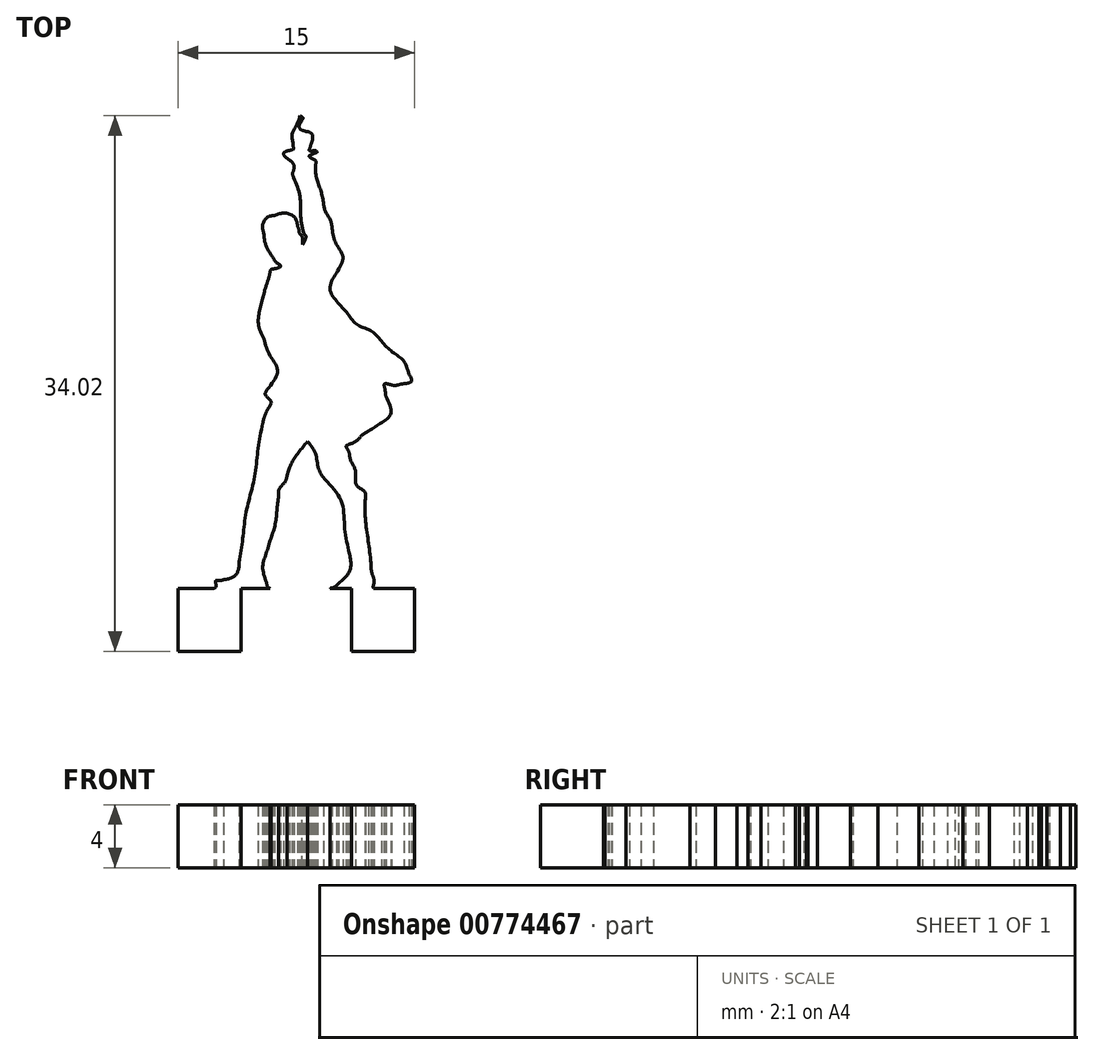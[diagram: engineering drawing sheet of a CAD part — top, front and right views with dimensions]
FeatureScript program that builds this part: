
annotation { "Feature Type Name" : "Feature", "Feature Type Description" : "" }
export const myFeature = defineFeature(function(context is Context, id is Id, definition is map)
    precondition{}
    {
        {
            var Q0;
            Q0=qCreatedBy(makeId("Top.planeOp"),FACE);
            var sketch = newSketch(context, id + "F0", { "sketchPlane" : qUnion([Q0])});
            skFitSpline(sketch, "E0", {"points": [v(-2.9, -14.64) * mm, v(-3.14, -13.66) * mm, v(-2.91, -12.76) * mm, v(-2.63, -11.83) * mm]});
            skFitSpline(sketch, "E1", {"points": [v(-2.63, -11.83) * mm, v(-2.36, -10.96) * mm, v(-2.24, -10.04) * mm, v(-2.13, -9.13) * mm]});
            skFitSpline(sketch, "E2", {"points": [v(-2.13, -9.13) * mm, v(-2.07, -8.64) * mm, v(-1.75, -8.28) * mm, v(-1.6, -7.84) * mm]});
            skFitSpline(sketch, "E3", {"points": [v(-1.6, -7.84) * mm, v(-1.32, -7.06) * mm, v(-0.86, -6.36) * mm, v(-0.3, -5.68) * mm]});
            skFitSpline(sketch, "E4", {"points": [v(-0.3, -5.68) * mm, v(0.23, -6.51) * mm, v(0.42, -7.46) * mm, v(0.97, -8.26) * mm]});
            skFitSpline(sketch, "E5", {"points": [v(0.97, -8.26) * mm, v(1.88, -9.56) * mm, v(2.06, -11.1) * mm, v(2.32, -12.62) * mm]});
            skFitSpline(sketch, "E6", {"points": [v(2.32, -12.62) * mm, v(2.46, -13.46) * mm, v(2.3, -14.07) * mm, v(1.67, -14.7) * mm]});
            skFitSpline(sketch, "E7", {"points": [v(1.67, -14.7) * mm, v(1.47, -14.9) * mm, v(1.3, -14.97) * mm, v(1.12, -15) * mm]});
            skFitSpline(sketch, "E8", {"points": [v(3.9, -15) * mm, v(3.88, -14.98) * mm, v(3.87, -14.94) * mm, v(3.88, -14.89) * mm]});
            skFitSpline(sketch, "E9", {"points": [v(3.88, -14.89) * mm, v(3.92, -14.44) * mm, v(3.79, -14.02) * mm, v(3.74, -13.58) * mm]});
            skFitSpline(sketch, "E10", {"points": [v(3.74, -13.58) * mm, v(3.6, -12.23) * mm, v(3.4, -10.87) * mm, v(3.35, -9.51) * mm]});
            skFitSpline(sketch, "E11", {"points": [v(3.35, -9.51) * mm, v(3.32, -8.87) * mm, v(2.83, -8.49) * mm, v(2.76, -7.9) * mm]});
            skFitSpline(sketch, "E12", {"points": [v(2.76, -7.9) * mm, v(2.71, -7.42) * mm, v(2.48, -6.98) * mm, v(2.36, -6.5) * mm]});
            skFitSpline(sketch, "E13", {"points": [v(2.36, -6.5) * mm, v(2.3, -6.28) * mm, v(2.16, -5.99) * mm, v(2.47, -5.82) * mm]});
            skFitSpline(sketch, "E14", {"points": [v(2.47, -5.82) * mm, v(2.88, -5.6) * mm, v(3.19, -5.26) * mm, v(3.58, -5.01) * mm]});
            skFitSpline(sketch, "E15", {"points": [v(3.58, -5.01) * mm, v(4.39, -4.5) * mm, v(5, -3.9) * mm, v(4.69, -2.82) * mm]});
            skFitSpline(sketch, "E16", {"points": [v(4.69, -2.82) * mm, v(4.66, -2.74) * mm, v(4.66, -2.65) * mm, v(4.65, -2.57) * mm]});
            skFitSpline(sketch, "E17", {"points": [v(4.65, -2.57) * mm, v(4.6, -2.27) * mm, v(4.58, -2.03) * mm, v(5.03, -2.09) * mm]});
            skFitSpline(sketch, "E18", {"points": [v(5.03, -2.09) * mm, v(5.29, -2.12) * mm, v(5.57, -2.06) * mm, v(5.84, -2) * mm]});
            skFitSpline(sketch, "E19", {"points": [v(5.84, -2) * mm, v(6.17, -1.95) * mm, v(6.32, -1.82) * mm, v(6.15, -1.42) * mm]});
            skFitSpline(sketch, "E20", {"points": [v(6.15, -1.42) * mm, v(5.77, -0.53) * mm, v(5.05, 0.04) * mm, v(4.4, 0.69) * mm]});
            skFitSpline(sketch, "E21", {"points": [v(4.4, 0.69) * mm, v(3.74, 1.34) * mm, v(2.88, 1.73) * mm, v(2.26, 2.43) * mm]});
            skFitSpline(sketch, "E22", {"points": [v(2.26, 2.43) * mm, v(1.59, 3.19) * mm, v(1.13, 4.02) * mm, v(1.53, 5.03) * mm]});
            skFitSpline(sketch, "E23", {"points": [v(1.53, 5.03) * mm, v(1.94, 6.04) * mm, v(1.5, 6.93) * mm, v(1.27, 7.84) * mm]});
            skFitSpline(sketch, "E24", {"points": [v(1.27, 7.84) * mm, v(1.14, 8.4) * mm, v(0.84, 8.94) * mm, v(0.71, 9.5) * mm]});
            skFitSpline(sketch, "E25", {"points": [v(0.71, 9.5) * mm, v(0.53, 10.3) * mm, v(0.26, 11.1) * mm, v(0.22, 11.92) * mm]});
            skFitSpline(sketch, "E26", {"points": [v(0.22, 11.92) * mm, v(0.21, 12.16) * mm, v(-0.19, 12.42) * mm, v(0.25, 12.66) * mm]});
            skFitSpline(sketch, "E27", {"points": [v(0.25, 12.66) * mm, v(0.32, 12.7) * mm, v(0.2, 12.8) * mm, v(0.12, 12.8) * mm]});
            skFitSpline(sketch, "E28", {"points": [v(0.12, 12.8) * mm, v(-0.18, 12.8) * mm, v(-0.15, 12.94) * mm, v(-0.09, 13.16) * mm]});
            skFitSpline(sketch, "E29", {"points": [v(-0.09, 13.16) * mm, v(0.03, 13.54) * mm, v(-0.02, 13.86) * mm, v(-0.45, 14.03) * mm]});
            skFitSpline(sketch, "E30", {"points": [v(-0.45, 14.03) * mm, v(-0.73, 14.14) * mm, v(-0.83, 14.35) * mm, v(-0.7, 14.65) * mm]});
            skFitSpline(sketch, "E31", {"points": [v(-0.7, 14.65) * mm, v(-0.65, 14.74) * mm, v(-0.58, 14.86) * mm, v(-0.78, 15) * mm]});
            skFitSpline(sketch, "E32", {"points": [v(-0.78, 15) * mm, v(-0.98, 14.43) * mm, v(-1.26, 13.9) * mm, v(-1.23, 13.32) * mm]});
            skFitSpline(sketch, "E33", {"points": [v(-1.23, 13.32) * mm, v(-1.21, 13.06) * mm, v(-1.18, 12.9) * mm, v(-1.43, 12.8) * mm]});
            skFitSpline(sketch, "E34", {"points": [v(-1.43, 12.8) * mm, v(-1.8, 12.66) * mm, v(-1.75, 12.43) * mm, v(-1.5, 12.24) * mm]});
            skFitSpline(sketch, "E35", {"points": [v(-1.5, 12.24) * mm, v(-1.24, 12.01) * mm, v(-1.15, 11.74) * mm, v(-1.23, 11.42) * mm]});
            skFitSpline(sketch, "E36", {"points": [v(-1.23, 11.42) * mm, v(-1.26, 11.3) * mm, v(-1.22, 11.2) * mm, v(-1.18, 11.08) * mm]});
            skFitSpline(sketch, "E37", {"points": [v(-1.18, 11.08) * mm, v(-0.79, 9.94) * mm, v(-0.74, 8.73) * mm, v(-0.55, 7.55) * mm]});
            skFitSpline(sketch, "E38", {"points": [v(-0.55, 7.55) * mm, v(-0.4, 7.36) * mm, v(-0.43, 7.17) * mm, v(-0.6, 6.83) * mm]});
            skFitSpline(sketch, "E39", {"points": [v(-0.6, 6.83) * mm, v(-0.62, 7.1) * mm, v(-0.63, 7.23) * mm, v(-0.64, 7.36) * mm]});
            skFitSpline(sketch, "E40", {"points": [v(-0.64, 7.36) * mm, v(-0.8, 7.54) * mm, v(-0.85, 7.78) * mm, v(-0.93, 8) * mm]});
            skFitSpline(sketch, "E41", {"points": [v(-0.93, 8) * mm, v(-1.1, 8.54) * mm, v(-1.73, 8.82) * mm, v(-2.4, 8.66) * mm]});
            skFitSpline(sketch, "E42", {"points": [v(-2.4, 8.66) * mm, v(-2.85, 8.56) * mm, v(-3.15, 8.09) * mm, v(-3.08, 7.55) * mm]});
            skFitSpline(sketch, "E43", {"points": [v(-3.08, 7.55) * mm, v(-3, 6.98) * mm, v(-2.79, 6.46) * mm, v(-2.48, 5.99) * mm]});
            skFitSpline(sketch, "E44", {"points": [v(-2.48, 5.99) * mm, v(-2.3, 5.71) * mm, v(-2, 5.45) * mm, v(-2.56, 5.26) * mm]});
            skFitSpline(sketch, "E45", {"points": [v(-2.56, 5.26) * mm, v(-2.63, 5.23) * mm, v(-2.67, 5.09) * mm, v(-2.7, 5) * mm]});
            skFitSpline(sketch, "E46", {"points": [v(-2.7, 5) * mm, v(-2.82, 4.54) * mm, v(-2.97, 4.09) * mm, v(-3.08, 3.63) * mm]});
            skFitSpline(sketch, "E47", {"points": [v(-3.08, 3.63) * mm, v(-3.33, 2.68) * mm, v(-3.42, 1.78) * mm, v(-3.07, 0.83) * mm]});
            skFitSpline(sketch, "E48", {"points": [v(-3.07, 0.83) * mm, v(-2.7, -0.16) * mm, v(-2.2, -1.17) * mm, v(-2.75, -2.26) * mm]});
            skFitSpline(sketch, "E49", {"points": [v(-2.75, -2.26) * mm, v(-2.97, -2.7) * mm, v(-2.6, -3.14) * mm, v(-2.8, -3.58) * mm]});
            skFitSpline(sketch, "E50", {"points": [v(-2.8, -3.58) * mm, v(-2.95, -3.89) * mm, v(-3.07, -4.21) * mm, v(-3.14, -4.54) * mm]});
            skFitSpline(sketch, "E51", {"points": [v(-3.14, -4.54) * mm, v(-3.43, -6.05) * mm, v(-3.6, -7.57) * mm, v(-3.93, -9.08) * mm]});
            skFitSpline(sketch, "E52", {"points": [v(-3.93, -9.08) * mm, v(-4.25, -10.48) * mm, v(-4.42, -11.92) * mm, v(-4.63, -13.35) * mm]});
            skFitSpline(sketch, "E53", {"points": [v(-4.63, -13.35) * mm, v(-4.72, -13.95) * mm, v(-5.04, -14.3) * mm, v(-5.61, -14.46) * mm]});
            skFitSpline(sketch, "E54", {"points": [v(-5.61, -14.46) * mm, v(-5.8, -14.5) * mm, v(-6.12, -14.52) * mm, v(-6.12, -14.73) * mm]});
            skFitSpline(sketch, "E55", {"points": [v(-6.12, -14.73) * mm, v(-6.12, -14.9) * mm, v(-6.16, -14.97) * mm, v(-6.22, -15) * mm]});
            skLineSegment(sketch, "E56", {"start": v(1.12, -15) * mm, "end": v(3.9, -15) * mm});
            skFitSpline(sketch, "E57", {"points": [v(-2.69, -15) * mm, v(-2.8, -14.96) * mm, v(-2.86, -14.85) * mm, v(-2.9, -14.64) * mm]});
            skLineSegment(sketch, "E58", {"start": v(-6.22, -15) * mm, "end": v(-2.69, -15) * mm});
            skLineSegment(sketch, "E59.bottom", {"start": v(-8.51, -15) * mm, "end": v(-4.51, -15) * mm});
            skLineSegment(sketch, "E59.top", {"start": v(-8.51, -19) * mm, "end": v(-4.51, -19) * mm});
            skLineSegment(sketch, "E59.left", {"start": v(-8.51, -15) * mm, "end": v(-8.51, -19) * mm});
            skLineSegment(sketch, "E59.right", {"start": v(-4.51, -15) * mm, "end": v(-4.51, -19) * mm});
            skLineSegment(sketch, "E60.bottom", {"start": v(2.49, -15) * mm, "end": v(6.49, -15) * mm});
            skLineSegment(sketch, "E60.top", {"start": v(2.49, -19) * mm, "end": v(6.49, -19) * mm});
            skLineSegment(sketch, "E60.left", {"start": v(2.49, -15) * mm, "end": v(2.49, -19) * mm});
            skLineSegment(sketch, "E60.right", {"start": v(6.49, -15) * mm, "end": v(6.49, -19) * mm});
            skSolve(sketch);
        }
        {
            var Q0;
            Q0 = qSketchRegion(id + "F0", true);
            extrude(context, id + "F1", {"entities" : qUnion([Q0]), "endBound" : BoundingType.SYMMETRIC, "depth" : 4 * mm, "offsetDistance" : 25 * mm});
        }
    });
